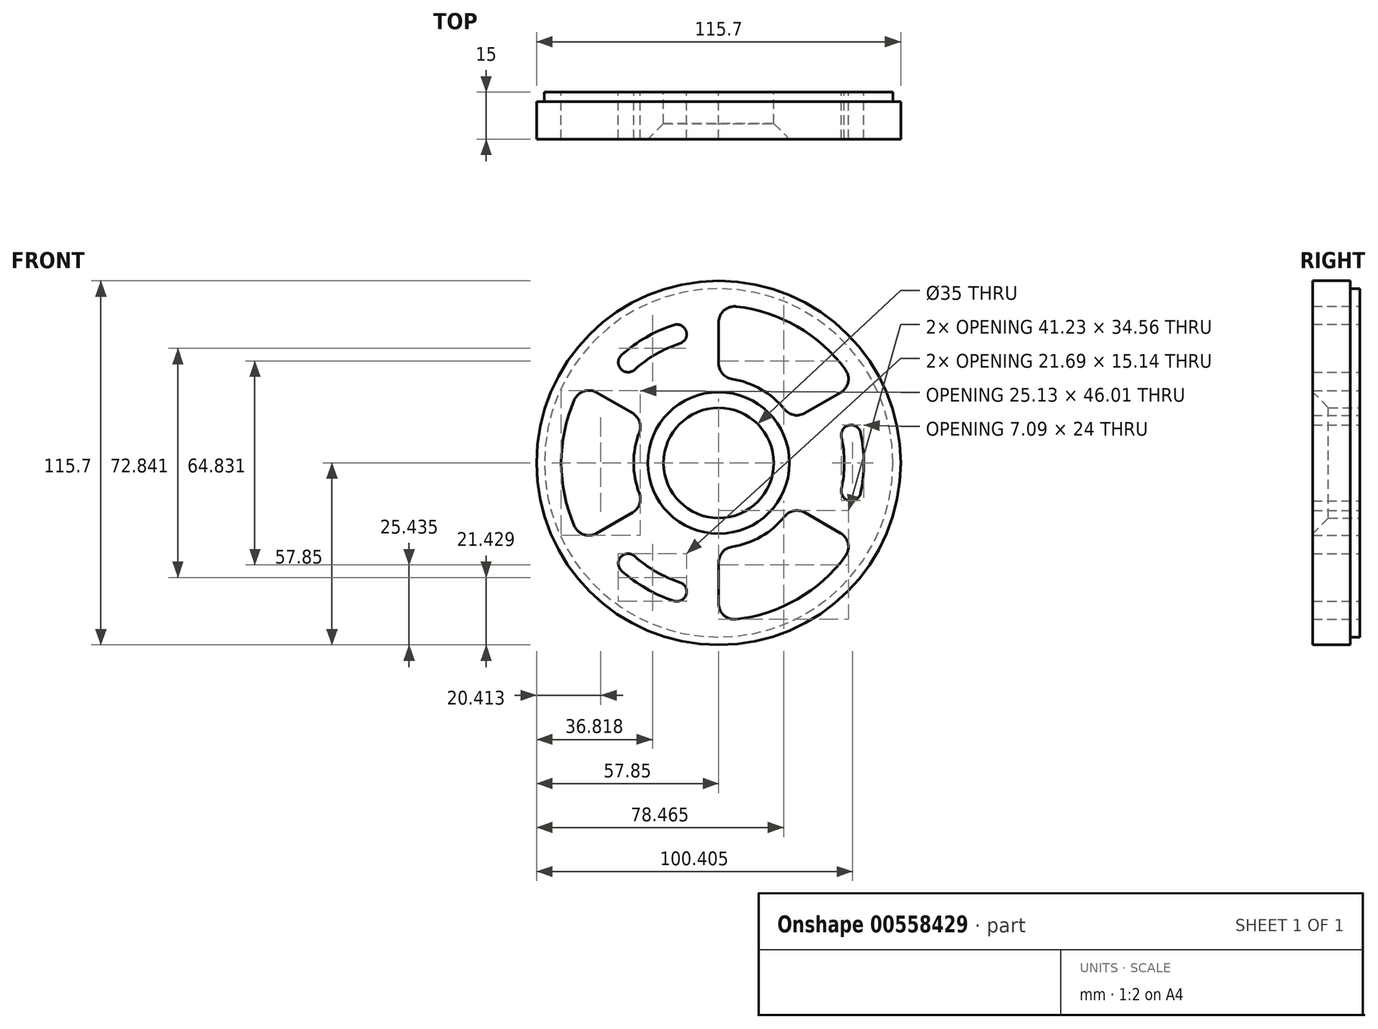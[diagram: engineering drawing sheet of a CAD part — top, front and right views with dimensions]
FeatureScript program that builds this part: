
annotation { "Feature Type Name" : "Feature", "Feature Type Description" : "" }
export const myFeature = defineFeature(function(context is Context, id is Id, definition is map)
    precondition{}
    {
        {
            var Q0;
            Q0=qCreatedBy(makeId("Front.planeOp"),FACE);
            var sketch = newSketch(context, id + "F0", { "sketchPlane" : qUnion([Q0])});
            skCircle(sketch, "E0", {"center": v(0, 0) * mm, "radius": 57.85 * mm});
            skCircle(sketch, "E1", {"center": v(0, 0) * mm, "radius": 17.5 * mm});
            skArc(sketch, "E2", {"start": v(45.1, -9.6) * mm, "mid": v(46.1, 0) * mm, "end": v(45.1, 9.6) * mm});
            skArc(sketch, "E3", {"start": v(39.03, -8.3) * mm, "mid": v(39.9, 0) * mm, "end": v(39.03, 8.3) * mm});
            skArc(sketch, "E4", {"start": v(45.1, 9.6) * mm, "mid": v(41.41, 11.98) * mm, "end": v(39.03, 8.3) * mm});
            skArc(sketch, "E5", {"start": v(39.03, -8.3) * mm, "mid": v(41.41, -11.98) * mm, "end": v(45.1, -9.6) * mm});
            skArc(sketch, "E6.MirrorCS", {"start": v(-14.23, 43.85) * mm, "mid": v(-10.33, 41.86) * mm, "end": v(-12.32, 37.95) * mm});
            skArc(sketch, "E7.MirrorCS", {"start": v(-30.86, 34.25) * mm, "mid": v(-23.05, 39.92) * mm, "end": v(-14.23, 43.85) * mm});
            skArc(sketch, "E8.MirrorCS", {"start": v(-26.7, 29.64) * mm, "mid": v(-19.95, 34.55) * mm, "end": v(-12.32, 37.95) * mm});
            skArc(sketch, "E9.MirrorCS", {"start": v(-26.7, 29.64) * mm, "mid": v(-31.08, 29.87) * mm, "end": v(-30.86, 34.25) * mm});
            skArc(sketch, "E10.MirrorCS", {"start": v(-14.23, -43.85) * mm, "mid": v(-23.05, -39.92) * mm, "end": v(-30.86, -34.25) * mm});
            skArc(sketch, "E11.MirrorCS", {"start": v(-12.32, -37.95) * mm, "mid": v(-19.95, -34.55) * mm, "end": v(-26.7, -29.64) * mm});
            skArc(sketch, "E12.MirrorCS", {"start": v(-30.86, -34.25) * mm, "mid": v(-31.08, -29.87) * mm, "end": v(-26.7, -29.64) * mm});
            skArc(sketch, "E13.MirrorCS", {"start": v(-12.32, -37.95) * mm, "mid": v(-10.33, -41.86) * mm, "end": v(-14.23, -43.85) * mm});
            skArc(sketch, "E14", {"start": v(-25.2, 9.68) * mm, "mid": v(-27, 0) * mm, "end": v(-25.2, -9.68) * mm});
            skArc(sketch, "E15", {"start": v(-45.81, 20.03) * mm, "mid": v(-50, 0) * mm, "end": v(-45.81, -20.03) * mm});
            skLineSegment(sketch, "E16.trimOffspring", {"start": v(-27.37, 15.8) * mm, "end": v(-38.73, 22.36) * mm});
            skLineSegment(sketch, "E17.trimOffspring", {"start": v(-27.37, -15.8) * mm, "end": v(-38.73, -22.36) * mm});
            skPoint(sketch, "E18.visualSharp", {"position": v(-23.38, 13.5) * mm});
            skArc(sketch, "E18.filletArc", {"start": v(-25.2, 9.68) * mm, "mid": v(-25.16, 13.14) * mm, "end": v(-27.37, 15.8) * mm});
            skPoint(sketch, "E19.visualSharp", {"position": v(-43.3, 25) * mm});
            skArc(sketch, "E19.filletArc", {"start": v(-38.73, 22.36) * mm, "mid": v(-42.8, 22.78) * mm, "end": v(-45.81, 20.03) * mm});
            skPoint(sketch, "E20.visualSharp", {"position": v(-43.3, -25) * mm});
            skArc(sketch, "E20.filletArc", {"start": v(-45.81, -20.03) * mm, "mid": v(-42.8, -22.78) * mm, "end": v(-38.73, -22.36) * mm});
            skPoint(sketch, "E21.visualSharp", {"position": v(-23.38, -13.5) * mm});
            skArc(sketch, "E21.filletArc", {"start": v(-27.37, -15.8) * mm, "mid": v(-25.16, -13.14) * mm, "end": v(-25.2, -9.68) * mm});
            skArc(sketch, "E22.MirrorCS", {"start": v(0, -31.6) * mm, "mid": v(1.2, -28.36) * mm, "end": v(4.22, -26.67) * mm});
            skArc(sketch, "E23.MirrorCS", {"start": v(20.99, -16.99) * mm, "mid": v(23.96, -15.22) * mm, "end": v(27.37, -15.8) * mm});
            skArc(sketch, "E24.MirrorCS", {"start": v(5.56, -49.7) * mm, "mid": v(1.67, -48.45) * mm, "end": v(0, -44.72) * mm});
            skPoint(sketch, "E25.MirrorP", {"position": v(23.38, -13.5) * mm});
            skLineSegment(sketch, "E26.MirrorCS", {"start": v(27.37, -15.8) * mm, "end": v(38.73, -22.36) * mm});
            skPoint(sketch, "E27.MirrorP", {"position": v(0, -50) * mm});
            skPoint(sketch, "E28.MirrorP", {"position": v(0, -27) * mm});
            skArc(sketch, "E29.MirrorCS", {"start": v(20.99, -16.99) * mm, "mid": v(13.5, -23.38) * mm, "end": v(4.22, -26.67) * mm});
            skLineSegment(sketch, "E30.MirrorCS", {"start": v(0, -31.6) * mm, "end": v(0, -44.72) * mm});
            skArc(sketch, "E31.MirrorCS", {"start": v(38.73, -22.36) * mm, "mid": v(41.12, -25.67) * mm, "end": v(40.26, -29.66) * mm});
            skArc(sketch, "E32.MirrorCS", {"start": v(40.26, -29.66) * mm, "mid": v(25, -43.3) * mm, "end": v(5.56, -49.7) * mm});
            skArc(sketch, "E33.MirrorCS", {"start": v(4.22, 26.67) * mm, "mid": v(1.2, 28.36) * mm, "end": v(0, 31.6) * mm});
            skArc(sketch, "E34.MirrorCS", {"start": v(0, 44.72) * mm, "mid": v(1.67, 48.45) * mm, "end": v(5.56, 49.7) * mm});
            skArc(sketch, "E35.MirrorCS", {"start": v(40.26, 29.66) * mm, "mid": v(41.12, 25.67) * mm, "end": v(38.73, 22.36) * mm});
            skArc(sketch, "E36.MirrorCS", {"start": v(4.22, 26.67) * mm, "mid": v(13.5, 23.38) * mm, "end": v(20.99, 16.99) * mm});
            skArc(sketch, "E37.MirrorCS", {"start": v(5.56, 49.7) * mm, "mid": v(25, 43.3) * mm, "end": v(40.26, 29.66) * mm});
            skPoint(sketch, "E38.MirrorP", {"position": v(0, 50) * mm});
            skLineSegment(sketch, "E39.MirrorCS", {"start": v(27.37, 15.8) * mm, "end": v(38.73, 22.36) * mm});
            skArc(sketch, "E40.MirrorCS", {"start": v(27.37, 15.8) * mm, "mid": v(23.96, 15.22) * mm, "end": v(20.99, 16.99) * mm});
            skLineSegment(sketch, "E41.MirrorCS", {"start": v(0, 31.6) * mm, "end": v(0, 44.72) * mm});
            skPoint(sketch, "E42.MirrorP", {"position": v(43.3, 25) * mm});
            skSolve(sketch);
        }
        {
            var Q0;
            Q0=makeQuery(id+"F0.imprint","IMPRINT",FACE,{"disambiguationData":[TD([[makeQuery(id+"F0.imprint","IMPRINT",EDGE,{"derivedFrom":sQuery(id+"F0.wireOp",EDGE,"E0")}),1.0]])]});
            extrude(context, id + "F1", {"entities" : qUnion([Q0]), "depth" : 15 * mm, "offsetDistance" : 25 * mm});
        }
        {
            var Q0;
            Q0=makeQuery(id+"F1.opExtrude","CAP_FACE",FACE,{"disambiguationData":[OSD([sQuery(id+"F0.wireOp",EDGE,"E0"),sQuery(id+"F0.wireOp",EDGE,"QBD5CPNR-eTBn-mDMN-URER-3Hg85SiTSXXa")])],"isStart":true});
            var sketch = newSketch(context, id + "F2", { "sketchPlane" : qUnion([Q0])});
            skCircle(sketch, "E43", {"center": v(0, 0) * mm, "radius": 55.35 * mm});
            skCircle(sketch, "E44", {"center": v(0, 0) * mm, "radius": 57.85 * mm});
            skSolve(sketch);
        }
        {
            var Q0;
            Q0=makeQuery(id+"F2.imprint","IMPRINT",FACE,{"disambiguationData":[TD([[makeQuery(id+"F2.imprint","IMPRINT",EDGE,{"derivedFrom":sQuery(id+"F2.wireOp",EDGE,"E43")}),-1.0]])]});
            extrude(context, id + "F3", {"entities" : qUnion([Q0]), "operationType" : NewBodyOperationType.REMOVE, "oppositeDirection" : true, "depth" : 3 * mm, "offsetDistance" : 25 * mm});
        }
        {
            var Q0;
            Q0=makeQuery(id+"F1.opExtrude","CAP_EDGE",EDGE,{"disambiguationData":[OSD([sQuery(id+"F0.wireOp",EDGE,"E1")])],"isStart":false});
            chamfer(context, id + "F4", {"entities" : qUnion([Q0]), "width" : 5 * mm, "tangentPropagation" : true});
        }
    });
